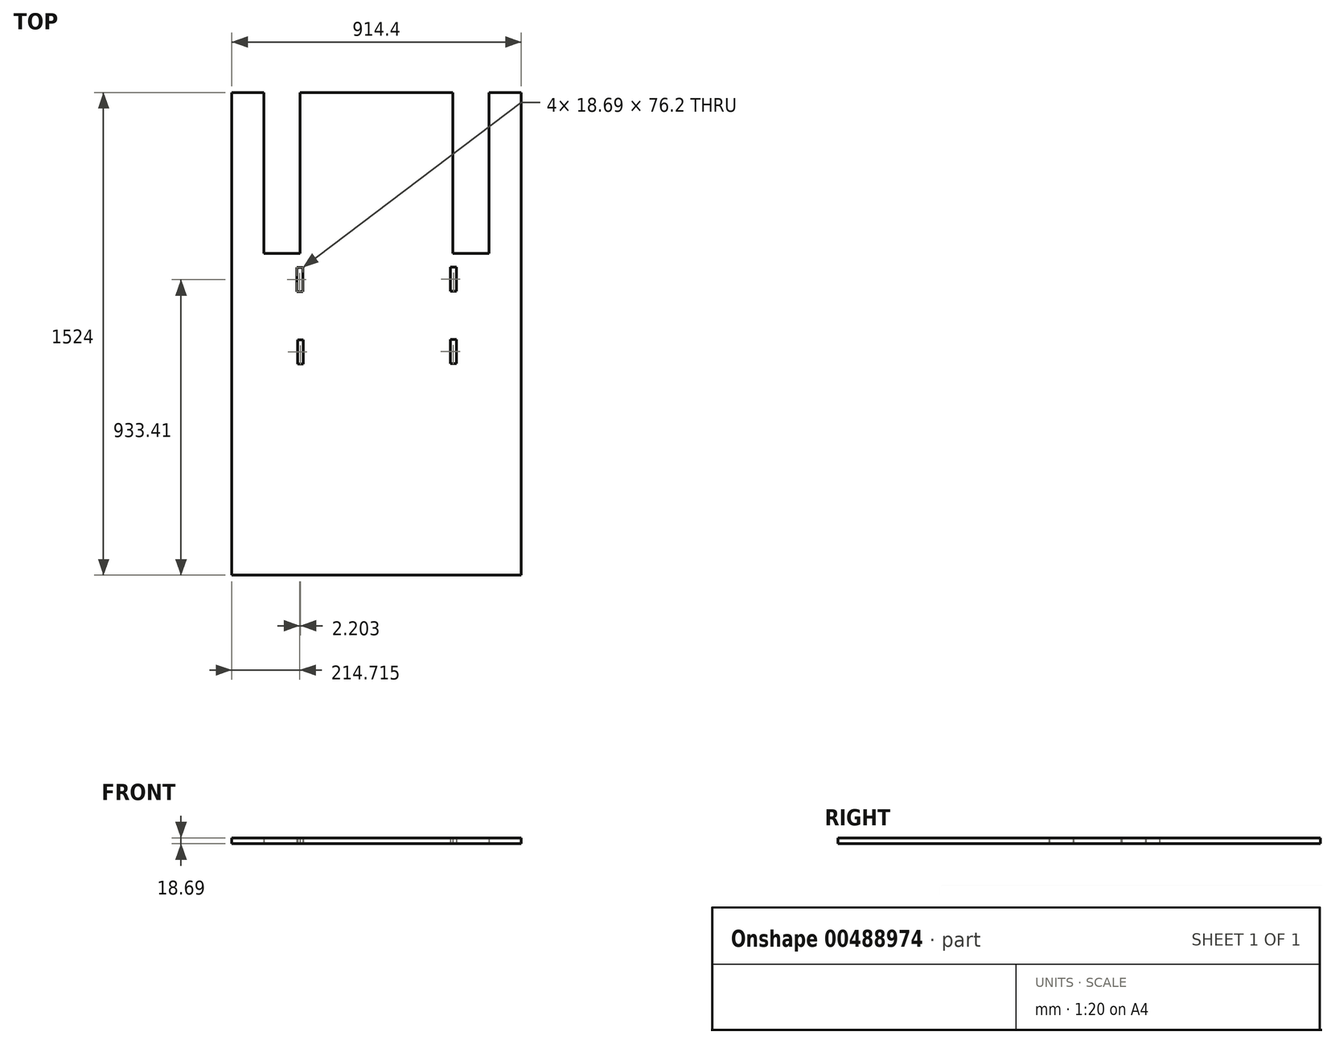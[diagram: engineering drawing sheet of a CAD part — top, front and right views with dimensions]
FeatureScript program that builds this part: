
annotation { "Feature Type Name" : "Feature", "Feature Type Description" : "" }
export const myFeature = defineFeature(function(context is Context, id is Id, definition is map)
    precondition{}
    {
        {
            var Q0;
            Q0=qCreatedBy(makeId("Top.planeOp"),FACE);
            var sketch = newSketch(context, id + "F0", { "sketchPlane" : qUnion([Q0])});
            skLineSegment(sketch, "E0.bottom", {"start": v(-1094.66, 1070.43) * mm, "end": v(-180.26, 1070.43) * mm});
            skLineSegment(sketch, "E0.top", {"start": v(-1094.66, -453.57) * mm, "end": v(-180.26, -453.57) * mm});
            skLineSegment(sketch, "E0.left", {"start": v(-1094.66, 1070.43) * mm, "end": v(-1094.66, -453.57) * mm});
            skLineSegment(sketch, "E0.right", {"start": v(-180.26, 1070.43) * mm, "end": v(-180.26, -453.57) * mm});
            skLineSegment(sketch, "E1.top", {"start": v(-993.06, 562.43) * mm, "end": v(-878.76, 562.43) * mm});
            skLineSegment(sketch, "E1.left", {"start": v(-993.06, 1070.43) * mm, "end": v(-993.06, 562.43) * mm});
            skLineSegment(sketch, "E1.right", {"start": v(-878.76, 1070.43) * mm, "end": v(-878.76, 562.43) * mm});
            skLineSegment(sketch, "E2.top", {"start": v(-396.16, 562.43) * mm, "end": v(-281.86, 562.43) * mm});
            skLineSegment(sketch, "E2.left", {"start": v(-396.16, 1070.43) * mm, "end": v(-396.16, 562.43) * mm});
            skLineSegment(sketch, "E2.right", {"start": v(-281.86, 1070.43) * mm, "end": v(-281.86, 562.43) * mm});
            skLineSegment(sketch, "E3.bottom", {"start": v(-889.3, 517.94) * mm, "end": v(-870.6, 517.94) * mm});
            skLineSegment(sketch, "E3.top", {"start": v(-889.3, 441.74) * mm, "end": v(-870.6, 441.74) * mm});
            skLineSegment(sketch, "E3.left", {"start": v(-870.6, 517.94) * mm, "end": v(-870.6, 441.74) * mm});
            skLineSegment(sketch, "E3.right", {"start": v(-889.3, 517.94) * mm, "end": v(-889.3, 441.74) * mm});
            skLineSegment(sketch, "E4", {"start": v(-878.76, 562.43) * mm, "end": v(-878.43, 206.83) * mm, "construction": true});
            skLineSegment(sketch, "E5.bottom", {"start": v(-403.83, 290.93) * mm, "end": v(-385.14, 290.93) * mm});
            skLineSegment(sketch, "E5.top", {"start": v(-403.83, 214.73) * mm, "end": v(-385.14, 214.73) * mm});
            skLineSegment(sketch, "E5.left", {"start": v(-385.14, 290.93) * mm, "end": v(-385.14, 214.73) * mm});
            skLineSegment(sketch, "E5.right", {"start": v(-403.83, 290.93) * mm, "end": v(-403.83, 214.73) * mm});
            skLineSegment(sketch, "E6.bottom", {"start": v(-887.09, 289.34) * mm, "end": v(-868.4, 289.34) * mm});
            skLineSegment(sketch, "E6.top", {"start": v(-887.09, 213.14) * mm, "end": v(-868.4, 213.14) * mm});
            skLineSegment(sketch, "E6.left", {"start": v(-868.4, 289.34) * mm, "end": v(-868.4, 213.14) * mm});
            skLineSegment(sketch, "E6.right", {"start": v(-887.09, 289.34) * mm, "end": v(-887.09, 213.14) * mm});
            skLineSegment(sketch, "E7.bottom", {"start": v(-403.45, 519.53) * mm, "end": v(-384.76, 519.53) * mm});
            skLineSegment(sketch, "E7.top", {"start": v(-403.45, 443.33) * mm, "end": v(-384.76, 443.33) * mm});
            skLineSegment(sketch, "E7.left", {"start": v(-384.76, 519.53) * mm, "end": v(-384.76, 443.33) * mm});
            skLineSegment(sketch, "E7.right", {"start": v(-403.45, 519.53) * mm, "end": v(-403.45, 443.33) * mm});
            skLineSegment(sketch, "E8", {"start": v(-393.82, 561.79) * mm, "end": v(-393.5, 206.2) * mm, "construction": true});
            skSolve(sketch);
        }
        {
            var Q0;
            Q0=makeQuery(id+"F0.imprint","IMPRINT",FACE,{"disambiguationData":[TD([[makeQuery(id+"F0.imprint","IMPRINT",EDGE,{"derivedFrom":sQuery(id+"F0.wireOp",EDGE,"E0.bottom")}),-1.0]])]});
            extrude(context, id + "F1", {"entities" : qUnion([Q0]), "depth" : 18.7 * mm, "offsetDistance" : 25.4 * mm});
        }
    });
